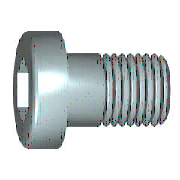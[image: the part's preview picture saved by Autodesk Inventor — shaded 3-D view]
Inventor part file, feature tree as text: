
AUTODESK INVENTOR PART (.ipt)
format: ipt  version: 2020 (Build 240168000, 168)  size: 184,832 bytes
history: native  units: mm (DEFAULTED — no unit token found)
features: sketch x2, chamfer x1, extrude x1, other x1, plane x1
ambient origin geometry x7: Origin, YZ Plane, XY Plane, X Axis, Y Axis, Z Axis, Center Point
bodies: Solid1 (feature_tree), Body (feature_tree)
feature tree (6):
  sketch  "Sketch1"  dims[d0=2.8mm]
  chamfer  "Chamfer2"  Angle=60.0deg  [1 undecoded]
  extrude  "Slot"  Depth=2.0mm
  other  "Work Axis1"
  plane  "Work Plane1"
  sketch  "Sketch2"  dims[d1=1.6mm d2=60.0deg d3=4.0mm d4=3.464102mm d5=7.0mm d10=90.0deg d11=10.0mm d6=0.0mm d7=14.0mm d8=0.0mm d9=0.429415mm d12=0.429415mm d14=0.0mm d15=3.3mm d16=2.0mm d17=50.0mm d28=45.0deg d30=0.0mm d31=0.0mm d32=45.0deg d33=0.4mm d34=90.0deg]
note: 1 required parameter value undecoded (feature->parameter linkage not recoverable at this tier; creation-order binding heuristic only, values carry confidence <= 0.55)
